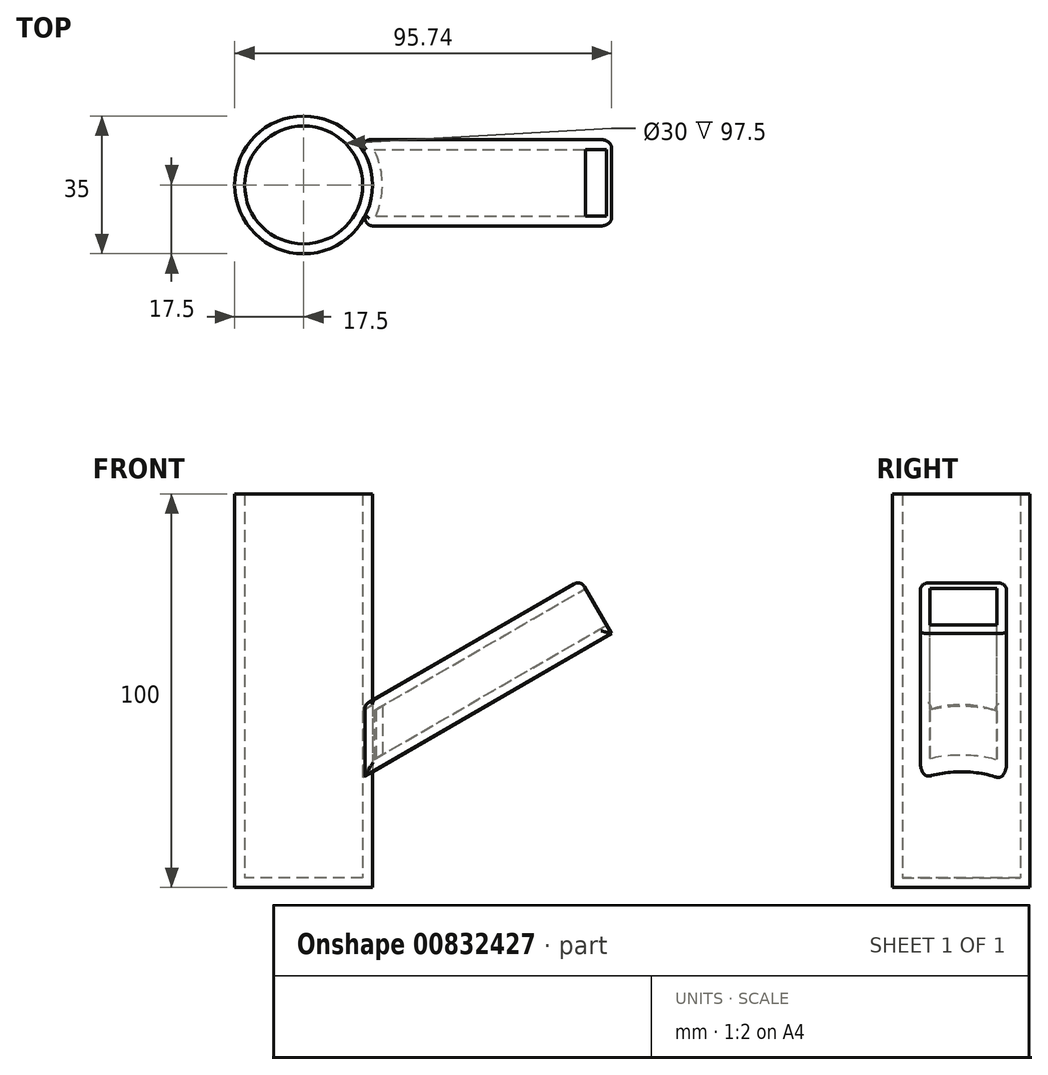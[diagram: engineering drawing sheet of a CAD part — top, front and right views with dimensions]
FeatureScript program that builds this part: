
annotation { "Feature Type Name" : "Feature", "Feature Type Description" : "" }
export const myFeature = defineFeature(function(context is Context, id is Id, definition is map)
    precondition{}
    {
        {
            var Q0;
            Q0=qCreatedBy(makeId("Top.planeOp"),FACE);
            var sketch = newSketch(context, id + "F0", { "sketchPlane" : qUnion([Q0])});
            skCircle(sketch, "E0", {"center": v(0, 0) * mm, "radius": 17.5 * mm});
            skSolve(sketch);
        }
        {
            var Q0;
            Q0 = qSketchRegion(id + "F0", true);
            extrude(context, id + "F1", {"entities" : qUnion([Q0]), "depth" : 100 * mm, "offsetDistance" : 25 * mm});
        }
        {
            var Q0;
            Q0=qCreatedBy(makeId("Top.planeOp"),FACE);
            var sketch = newSketch(context, id + "F2", { "sketchPlane" : qUnion([Q0])});
            skLineSegment(sketch, "E1", {"start": v(0, 40.04) * mm, "end": v(0, -44.29) * mm});
            skSolve(sketch);
        }
        {
            var Q0;
            Q0 = qBodyType(qCreatedBy(id + "F2" ,EDGE), BodyType.WIRE);
            var Q1;
            Q1=qCreatedBy(makeId("Right.planeOp"),FACE);
            cPlane(context, id + "F3", {"entities" : qUnion([Q0, Q1]), "cplaneType" : CPlaneType.LINE_ANGLE, "offset" : 25 * mm, "angle" : 30 * degree, "width" : 150 * mm, "height" : 150 * mm});
        }
        {
            var Q0;
            Q0=qCreatedBy(id+"F3.planeOp",FACE);
            var sketch = newSketch(context, id + "F4", { "sketchPlane" : qUnion([Q0])});
            skLineSegment(sketch, "E2.bottom", {"start": v(10.42, 32.46) * mm, "end": v(-11.5, 32.46) * mm});
            skLineSegment(sketch, "E2.top", {"start": v(10.42, 16.72) * mm, "end": v(-11.5, 16.72) * mm});
            skLineSegment(sketch, "E2.left", {"start": v(10.42, 32.46) * mm, "end": v(10.42, 16.72) * mm});
            skLineSegment(sketch, "E2.right", {"start": v(-11.5, 32.46) * mm, "end": v(-11.5, 16.72) * mm});
            skSolve(sketch);
        }
        {
            var Q0;
            Q0 = qSketchRegion(id + "F4", true);
            extrude(context, id + "F5", {"entities" : qUnion([Q0]), "oppositeDirection" : true, "depth" : 100 * mm, "offsetDistance" : 25 * mm});
        }
        {
            var Q0;
            Q0=makeQuery(id+"F1.opExtrude","SWEPT_BODY",BODY,{"disambiguationData":[OSD([sQuery(id+"F0.wireOp",EDGE,"E0")])]});
            var Q1;
            Q1=makeQuery(id+"F5.opExtrude","SWEPT_BODY",BODY,{"disambiguationData":[OSD([sQuery(id+"F4.wireOp",EDGE,"E2.bottom"),sQuery(id+"F4.wireOp",EDGE,"E2.top"),sQuery(id+"F4.wireOp",EDGE,"E2.left"),sQuery(id+"F4.wireOp",EDGE,"E2.right")])]});
            booleanBodies(context, id + "F6", {"operationType" : BooleanOperationType.SUBTRACTION, "tools" : qUnion([Q0]), "targets" : qUnion([Q1]), "keepTools" : true});
        }
        {
            var Q0;
            Q0=makeQuery(id+"F6.opBoolean","SPLIT",BODY,{"disambiguationData":[OD(2.0)],"derivedFrom":makeQuery(id+"F5.opExtrude","SWEPT_BODY",BODY,{"disambiguationData":[OSD([sQuery(id+"F4.wireOp",EDGE,"E2.bottom"),sQuery(id+"F4.wireOp",EDGE,"E2.top"),sQuery(id+"F4.wireOp",EDGE,"E2.left"),sQuery(id+"F4.wireOp",EDGE,"E2.right")])]})});
            var Q1;
            Q1=makeQuery(id+"F6.opBoolean","SPLIT",BODY,{"disambiguationData":[OD(1.0)],"derivedFrom":makeQuery(id+"F5.opExtrude","SWEPT_BODY",BODY,{"disambiguationData":[OSD([sQuery(id+"F4.wireOp",EDGE,"E2.bottom"),sQuery(id+"F4.wireOp",EDGE,"E2.top"),sQuery(id+"F4.wireOp",EDGE,"E2.left"),sQuery(id+"F4.wireOp",EDGE,"E2.right")])]})});
            deleteBodies(context, id + "F7", {"entities" : qUnion([Q0, Q1])});
        }
        {
            var Q0;
            {var subQ0=sQuery(id+"F4.wireOp",EDGE,"E2.right");var subQ1=sQuery(id+"F4.wireOp",EDGE,"E2.left");var subQ2=sQuery(id+"F4.wireOp",EDGE,"E2.bottom");Q0=makeQuery(id+"F6.opBoolean","SPLIT",FACE,{"disambiguationData":[TD([makeQuery(id+"F1.opExtrude","SWEPT_FACE",FACE,{"disambiguationData":[OSD([sQuery(id+"F0.wireOp",EDGE,"E0")])]}),makeQuery(id+"F5.opExtrude","CAP_FACE",FACE,{"disambiguationData":[OSD([subQ2,sQuery(id+"F4.wireOp",EDGE,"E2.top"),subQ1,subQ0])],"isStart":false}),makeQuery(id+"F5.opExtrude","SWEPT_FACE",FACE,{"disambiguationData":[OSD([subQ1])]}),makeQuery(id+"F5.opExtrude","SWEPT_FACE",FACE,{"disambiguationData":[OSD([subQ0])]})])],"derivedFrom":makeQuery(id+"F5.opExtrude","SWEPT_FACE",FACE,{"disambiguationData":[OSD([subQ2])]})});}
            var Q1;
            {var subQ1=sQuery(id+"F4.wireOp",EDGE,"E2.left");var subQ2=sQuery(id+"F4.wireOp",EDGE,"E2.top");Q1=makeQuery(id+"F6.opBoolean","SPLIT",FACE,{"disambiguationData":[TD([makeQuery(id+"F5.opExtrude","SWEPT_FACE",FACE,{"disambiguationData":[OSD([subQ2])]})])],"derivedFrom":makeQuery(id+"F5.opExtrude","SWEPT_FACE",FACE,{"disambiguationData":[OSD([subQ1])]})});}
            var Q2;
            {var subQ1=sQuery(id+"F4.wireOp",EDGE,"E2.right");var subQ2=sQuery(id+"F4.wireOp",EDGE,"E2.top");Q2=makeQuery(id+"F6.opBoolean","SPLIT",FACE,{"disambiguationData":[TD([makeQuery(id+"F5.opExtrude","SWEPT_FACE",FACE,{"disambiguationData":[OSD([subQ2])]})])],"derivedFrom":makeQuery(id+"F5.opExtrude","SWEPT_FACE",FACE,{"disambiguationData":[OSD([subQ1])]})});}
            fillet(context, id + "F8", {"entities" : qUnion([Q0, Q1, Q2]), "radius" : 2 * mm, "tangentPropagation" : true, "allowEdgeOverflow" : false});
        }
        {
            var Q0;
            Q0=makeQuery(id+"F1.opExtrude","CAP_FACE",FACE,{"disambiguationData":[OSD([sQuery(id+"F0.wireOp",EDGE,"E0")])],"isStart":false});
            var Q1;
            Q1=makeQuery(id+"F5.opExtrude","CAP_FACE",FACE,{"disambiguationData":[OSD([sQuery(id+"F4.wireOp",EDGE,"E2.bottom"),sQuery(id+"F4.wireOp",EDGE,"E2.top"),sQuery(id+"F4.wireOp",EDGE,"E2.left"),sQuery(id+"F4.wireOp",EDGE,"E2.right")])],"isStart":false});
            shell(context, id + "F9", {"entities" : qUnion([Q0, Q1]), "thickness" : 2.5 * mm});
        }
    });
